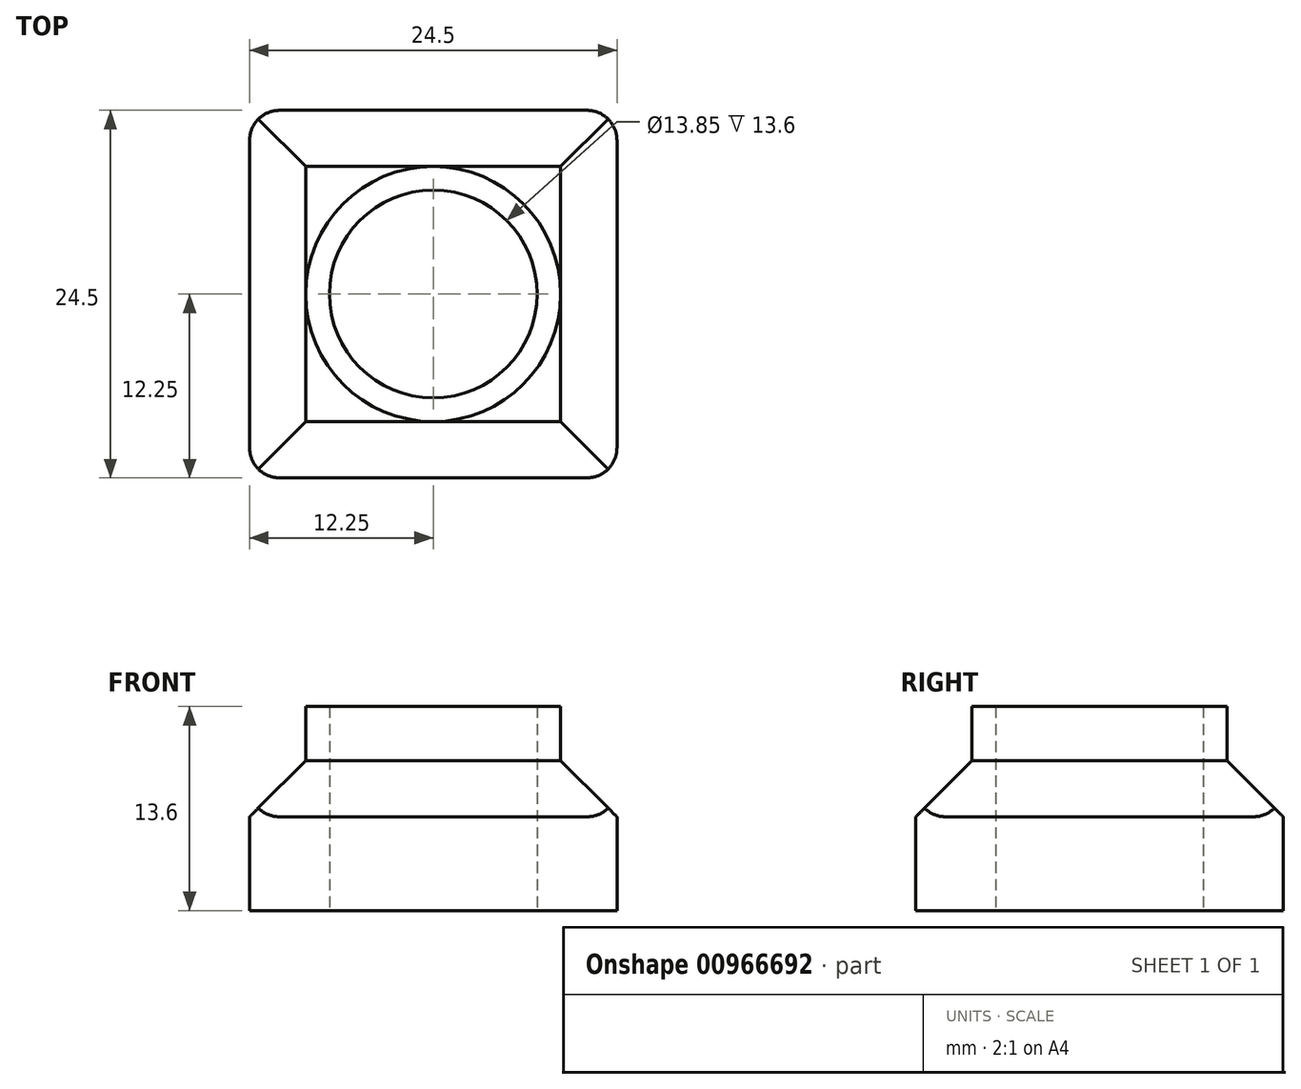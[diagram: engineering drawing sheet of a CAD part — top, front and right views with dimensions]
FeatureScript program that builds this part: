
annotation { "Feature Type Name" : "Feature", "Feature Type Description" : "" }
export const myFeature = defineFeature(function(context is Context, id is Id, definition is map)
    precondition{}
    {
        {
            var Q0;
            Q0=qCreatedBy(makeId("Top.planeOp"),FACE);
            var sketch = newSketch(context, id + "F0", { "sketchPlane" : qUnion([Q0])});
            skLineSegment(sketch, "E0.bottom", {"start": v(12.25, 12.25) * mm, "end": v(-12.25, 12.25) * mm});
            skLineSegment(sketch, "E0.top", {"start": v(12.25, -12.25) * mm, "end": v(-12.25, -12.25) * mm});
            skLineSegment(sketch, "E0.left", {"start": v(12.25, 12.25) * mm, "end": v(12.25, -12.25) * mm});
            skLineSegment(sketch, "E0.right", {"start": v(-12.25, 12.25) * mm, "end": v(-12.25, -12.25) * mm});
            skPoint(sketch, "E0.middle", {"position": v(0, 0) * mm});
            skCircle(sketch, "E1", {"center": v(0, 0) * mm, "radius": 8.5 * mm});
            skCircle(sketch, "E2", {"center": v(0, 0) * mm, "radius": 6.92 * mm});
            skSolve(sketch);
        }
        {
            var Q0;
            Q0=makeQuery(id+"F0.imprint","IMPRINT",FACE,{"disambiguationData":[TD([[makeQuery(id+"F0.imprint","IMPRINT",EDGE,{"derivedFrom":sQuery(id+"F0.wireOp",EDGE,"E0.bottom")}),1.0]])]});
            var Q1;
            Q1=makeQuery(id+"F0.imprint","IMPRINT",FACE,{"disambiguationData":[TD([[makeQuery(id+"F0.imprint","IMPRINT",EDGE,{"derivedFrom":sQuery(id+"F0.wireOp",EDGE,"E2")}),1.0]])]});
            var Q2;
            Q2=makeQuery(id+"F0.imprint","IMPRINT",FACE,{"disambiguationData":[TD([[makeQuery(id+"F0.imprint","IMPRINT",EDGE,{"derivedFrom":sQuery(id+"F0.wireOp",EDGE,"E1")}),1.0]])]});
            extrude(context, id + "F1", {"entities" : qUnion([Q0, Q1, Q2]), "oppositeDirection" : true, "depth" : 10 * mm, "offsetDistance" : 25 * mm});
        }
        {
            var Q0;
            Q0=makeQuery(id+"F0.imprint","IMPRINT",FACE,{"disambiguationData":[TD([[makeQuery(id+"F0.imprint","IMPRINT",EDGE,{"derivedFrom":sQuery(id+"F0.wireOp",EDGE,"E1")}),1.0]])]});
            extrude(context, id + "F2", {"entities" : qUnion([Q0]), "operationType" : NewBodyOperationType.ADD, "depth" : 3.6 * mm, "offsetDistance" : 25 * mm});
        }
        {
            var Q0;
            Q0=makeQuery(id+"F0.imprint","IMPRINT",FACE,{"disambiguationData":[TD([[makeQuery(id+"F0.imprint","IMPRINT",EDGE,{"derivedFrom":sQuery(id+"F0.wireOp",EDGE,"E2")}),1.0]])]});
            extrude(context, id + "F3", {"entities" : qUnion([Q0]), "operationType" : NewBodyOperationType.REMOVE, "oppositeDirection" : true, "depth" : 25 * mm, "offsetDistance" : 25 * mm});
        }
        {
            var Q0;
            Q0=makeQuery(id+"F1.opExtrude","CAP_EDGE",EDGE,{"disambiguationData":[OSD([sQuery(id+"F0.wireOp",EDGE,"E0.top")])],"isStart":true});
            var Q1;
            Q1=makeQuery(id+"F1.opExtrude","CAP_EDGE",EDGE,{"disambiguationData":[OSD([sQuery(id+"F0.wireOp",EDGE,"E0.left")])],"isStart":true});
            var Q2;
            Q2=makeQuery(id+"F1.opExtrude","CAP_EDGE",EDGE,{"disambiguationData":[OSD([sQuery(id+"F0.wireOp",EDGE,"E0.bottom")])],"isStart":true});
            var Q3;
            Q3=makeQuery(id+"F1.opExtrude","CAP_EDGE",EDGE,{"disambiguationData":[OSD([sQuery(id+"F0.wireOp",EDGE,"E0.right")])],"isStart":true});
            chamfer(context, id + "F4", {"entities" : qUnion([Q0, Q1, Q2, Q3]), "chamferType" : ChamferType.OFFSET_ANGLE, "width" : 3.75 * mm, "oppositeDirection" : false, "angle" : 45 * degree, "tangentPropagation" : true});
        }
        {
            var Q0;
            Q0=makeQuery(id+"F1.opExtrude","SWEPT_EDGE",EDGE,{"disambiguationData":[OSD([sQuery(id+"F0.wireOp",EDGE,"E0.top"),sQuery(id+"F0.wireOp",EDGE,"E0.left")])]});
            var Q1;
            Q1=makeQuery(id+"F1.opExtrude","SWEPT_EDGE",EDGE,{"disambiguationData":[OSD([sQuery(id+"F0.wireOp",EDGE,"E0.bottom"),sQuery(id+"F0.wireOp",EDGE,"E0.left")])]});
            var Q2;
            Q2=makeQuery(id+"F1.opExtrude","SWEPT_EDGE",EDGE,{"disambiguationData":[OSD([sQuery(id+"F0.wireOp",EDGE,"E0.bottom"),sQuery(id+"F0.wireOp",EDGE,"E0.right")])]});
            var Q3;
            Q3=makeQuery(id+"F1.opExtrude","SWEPT_EDGE",EDGE,{"disambiguationData":[OSD([sQuery(id+"F0.wireOp",EDGE,"E0.top"),sQuery(id+"F0.wireOp",EDGE,"E0.right")])]});
            fillet(context, id + "F5", {"entities" : qUnion([Q0, Q1, Q2, Q3]), "radius" : 2 * mm, "tangentPropagation" : true, "allowEdgeOverflow" : false});
        }
    });
